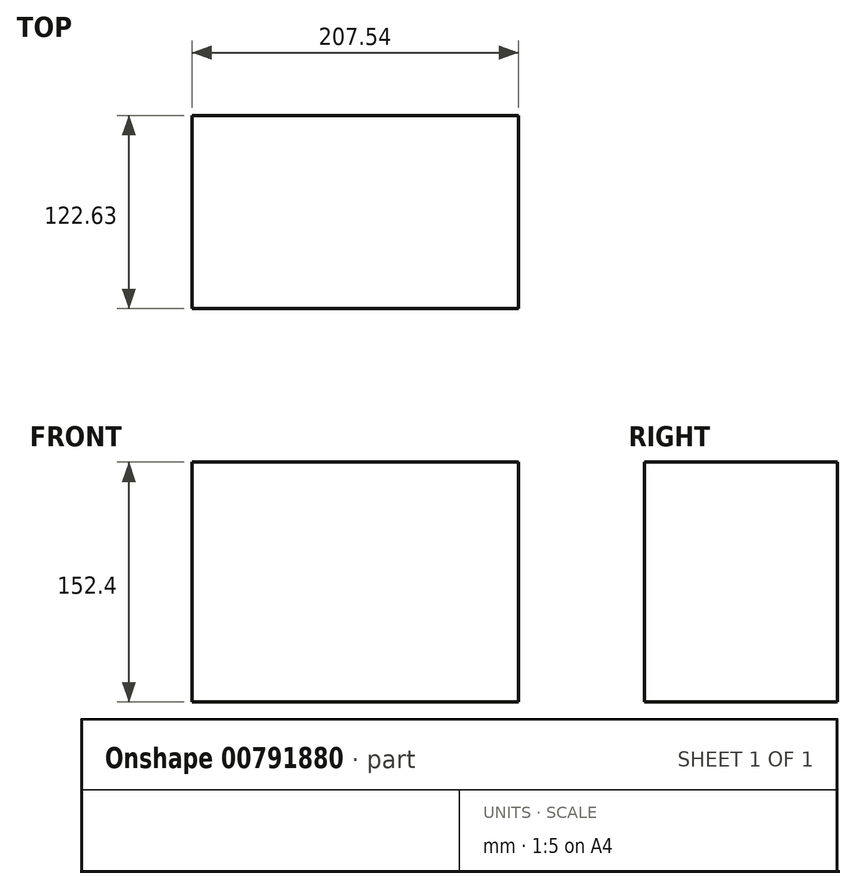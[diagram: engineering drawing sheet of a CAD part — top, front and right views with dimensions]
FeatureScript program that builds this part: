
annotation { "Feature Type Name" : "Feature", "Feature Type Description" : "" }
export const myFeature = defineFeature(function(context is Context, id is Id, definition is map)
    precondition{}
    {
        {
            var Q0;
            Q0=qCreatedBy(makeId("Top.planeOp"),FACE);
            var sketch = newSketch(context, id + "F0", { "sketchPlane" : qUnion([Q0])});
            skCircle(sketch, "E0", {"center": v(-311.54, 245.35) * mm, "radius": 63.5 * mm});
            skLineSegment(sketch, "E1.bottom", {"start": v(108.5, 232.64) * mm, "end": v(316.03, 232.64) * mm});
            skLineSegment(sketch, "E1.top", {"start": v(108.5, 110) * mm, "end": v(316.03, 110) * mm});
            skLineSegment(sketch, "E1.left", {"start": v(108.5, 232.64) * mm, "end": v(108.5, 110) * mm});
            skLineSegment(sketch, "E1.right", {"start": v(316.03, 232.64) * mm, "end": v(316.03, 110) * mm});
            skLineSegment(sketch, "E2", {"start": v(-335.96, -77.57) * mm, "end": v(-142.58, -143.6) * mm});
            skLineSegment(sketch, "E3", {"start": v(-142.58, -143.6) * mm, "end": v(-142.58, -336.98) * mm});
            skLineSegment(sketch, "E4", {"start": v(-142.58, -336.98) * mm, "end": v(-364.26, -372.36) * mm});
            skLineSegment(sketch, "E5", {"start": v(-364.26, -372.36) * mm, "end": v(-335.96, -77.57) * mm});
            skLineSegment(sketch, "E6", {"start": v(-277, -160.1) * mm, "end": v(-310.02, -292.17) * mm});
            skLineSegment(sketch, "E7", {"start": v(-310.02, -292.17) * mm, "end": v(-239, -309.93) * mm});
            skLineSegment(sketch, "E8", {"start": v(-239, -309.93) * mm, "end": v(-277, -160.1) * mm});
            skSolve(sketch);
        }
        {
            var Q0;
            Q0=makeQuery(id+"F0.imprint","IMPRINT",FACE,{"disambiguationData":[TD([[makeQuery(id+"F0.imprint","IMPRINT",EDGE,{"derivedFrom":sQuery(id+"F0.wireOp",EDGE,"E1.bottom")}),-1.0]])]});
            extrude(context, id + "F1", {"entities" : qUnion([Q0]), "depth" : 152.4 * mm, "offsetDistance" : 25.4 * mm});
        }
    });
